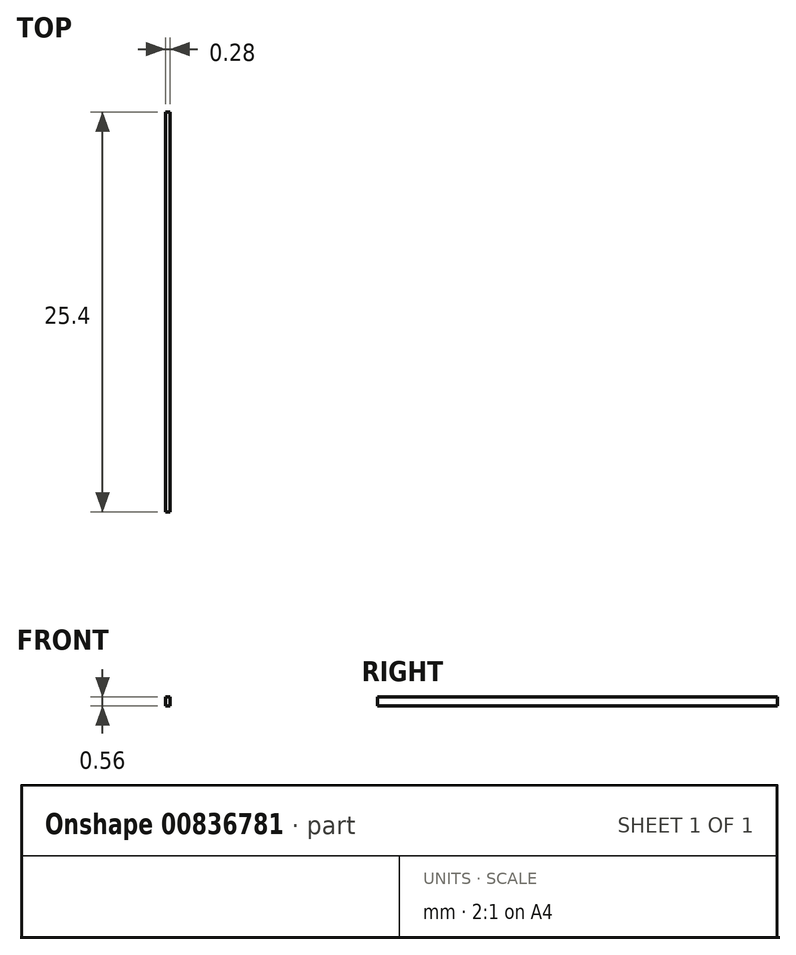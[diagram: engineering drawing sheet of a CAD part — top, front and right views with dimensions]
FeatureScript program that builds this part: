
annotation { "Feature Type Name" : "Feature", "Feature Type Description" : "" }
export const myFeature = defineFeature(function(context is Context, id is Id, definition is map)
    precondition{}
    {
        {
            var Q0;
            Q0=qCreatedBy(makeId("Front.planeOp"),FACE);
            var sketch = newSketch(context, id + "F0", { "sketchPlane" : qUnion([Q0])});
            skLineSegment(sketch, "E0.bottom", {"start": v(2.37, 0) * mm, "end": v(39.24, 0) * mm});
            skLineSegment(sketch, "E0.top", {"start": v(2.37, 17.04) * mm, "end": v(39.24, 17.04) * mm});
            skLineSegment(sketch, "E0.left", {"start": v(2.37, 0) * mm, "end": v(2.37, 17.04) * mm});
            skLineSegment(sketch, "E0.right", {"start": v(39.24, 0) * mm, "end": v(39.24, 17.04) * mm});
            skLineSegment(sketch, "E1.bottom", {"start": v(0, 0) * mm, "end": v(2.37, 0) * mm});
            skLineSegment(sketch, "E1.top", {"start": v(0, 0) * mm, "end": v(2.37, 0) * mm});
            skLineSegment(sketch, "E1.left", {"start": v(0, 0) * mm, "end": v(0, 0) * mm});
            skLineSegment(sketch, "E1.right", {"start": v(2.37, 0) * mm, "end": v(2.37, 0) * mm});
            skLineSegment(sketch, "E2.bottom", {"start": v(2.65, 0.56) * mm, "end": v(0, 0.56) * mm});
            skLineSegment(sketch, "E2.top", {"start": v(2.65, 0) * mm, "end": v(0, 0) * mm});
            skLineSegment(sketch, "E2.left", {"start": v(2.65, 0.56) * mm, "end": v(2.65, 0) * mm});
            skLineSegment(sketch, "E2.right", {"start": v(0, 0.56) * mm, "end": v(0, 0) * mm});
            skSolve(sketch);
        }
        {
            var Q0;
            Q0=makeQuery(id+"F0.imprint","IMPRINT",FACE,{"disambiguationData":[TD([[makeQuery(id+"F0.imprint","IMPRINT",EDGE,{"derivedFrom":sQuery(id+"F0.wireOp",EDGE,"E0.bottom")}),1.0]])]});
            extrude(context, id + "F1", {"entities" : qUnion([Q0]), "depth" : 25.4 * mm, "offsetDistance" : 25.4 * mm});
        }
    });
